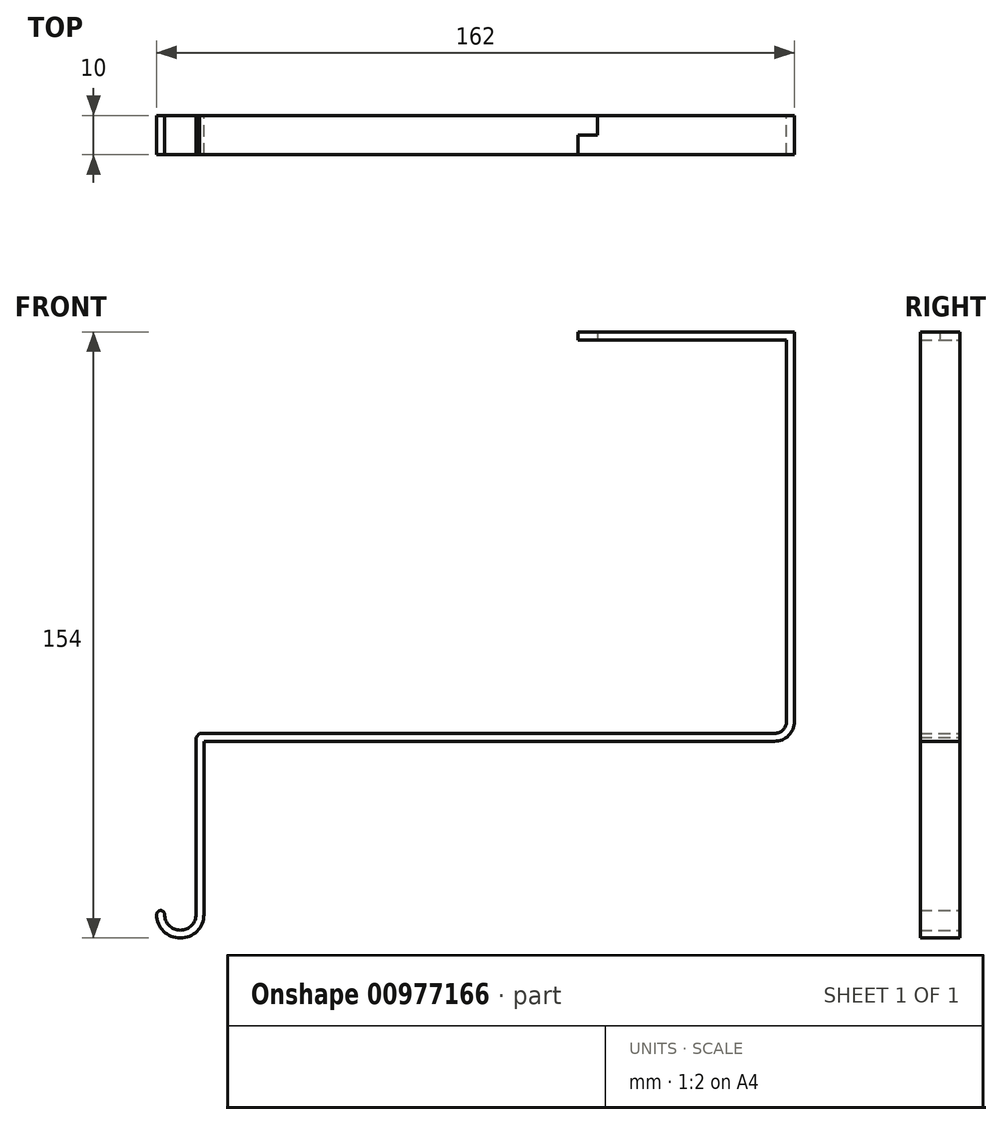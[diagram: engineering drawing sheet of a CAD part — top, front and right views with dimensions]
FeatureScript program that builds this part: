
annotation { "Feature Type Name" : "Feature", "Feature Type Description" : "" }
export const myFeature = defineFeature(function(context is Context, id is Id, definition is map)
    precondition{}
    {
        {
            var Q0;
            Q0=qCreatedBy(makeId("Front.planeOp"),FACE);
            var sketch = newSketch(context, id + "F0", { "sketchPlane" : qUnion([Q0])});
            skLineSegment(sketch, "E0", {"start": v(53.77, 110.57) * mm, "end": v(103.77, 110.57) * mm});
            skLineSegment(sketch, "E1", {"start": v(103.77, 110.57) * mm, "end": v(103.77, 11.57) * mm});
            skLineSegment(sketch, "E2", {"start": v(98.77, 6.57) * mm, "end": v(-46.23, 6.57) * mm});
            skLineSegment(sketch, "E3", {"start": v(-46.23, 6.57) * mm, "end": v(-46.23, -37.43) * mm});
            skArc(sketch, "E4", {"start": v(-46.23, -37.43) * mm, "mid": v(-52.23, -43.43) * mm, "end": v(-58.23, -37.43) * mm});
            skPoint(sketch, "E5.visualSharp", {"position": v(103.77, 6.57) * mm});
            skArc(sketch, "E5.filletArc", {"start": v(98.77, 6.57) * mm, "mid": v(102.3, 8.03) * mm, "end": v(103.77, 11.57) * mm});
            skLineSegment(sketch, "E6", {"start": v(53.77, 110.57) * mm, "end": v(48.77, 110.57) * mm});
            skLineSegment(sketch, "E7.0", {"start": v(-48.23, 7.5) * mm, "end": v(-48.23, -37.43) * mm});
            skLineSegment(sketch, "E7.1", {"start": v(53.77, 108.57) * mm, "end": v(48.77, 108.57) * mm});
            skLineSegment(sketch, "E7.2", {"start": v(53.77, 108.57) * mm, "end": v(101.77, 108.57) * mm});
            skLineSegment(sketch, "E7.3", {"start": v(101.77, 108.57) * mm, "end": v(101.77, 11.57) * mm});
            skLineSegment(sketch, "E7.4", {"start": v(98.77, 8.57) * mm, "end": v(-47.32, 8.57) * mm});
            skLineSegment(sketch, "E8", {"start": v(48.77, 110.57) * mm, "end": v(48.77, 108.57) * mm});
            skLineSegment(sketch, "E9", {"start": v(53.77, 110.57) * mm, "end": v(53.77, 108.57) * mm});
            skArc(sketch, "E10.0", {"start": v(-48.23, -37.43) * mm, "mid": v(-52.23, -41.43) * mm, "end": v(-56.23, -37.43) * mm});
            skArc(sketch, "E11", {"start": v(-58.23, -37.43) * mm, "mid": v(-57.23, -36.43) * mm, "end": v(-56.23, -37.43) * mm});
            skLineSegment(sketch, "E12", {"start": v(-47.32, 8.57) * mm, "end": v(-48.23, 7.5) * mm});
            skPoint(sketch, "E13.visualSharp", {"position": v(101.77, 8.57) * mm});
            skArc(sketch, "E13.filletArc", {"start": v(98.77, 8.57) * mm, "mid": v(100.9, 9.45) * mm, "end": v(101.77, 11.57) * mm});
            skSolve(sketch);
        }
        {
            var Q0;
            Q0=makeQuery(id+"F0.imprint","IMPRINT",FACE,{"disambiguationData":[TD([[makeQuery(id+"F0.imprint","IMPRINT",EDGE,{"derivedFrom":sQuery(id+"F0.wireOp",EDGE,"E0")}),-1.0]])]});
            extrude(context, id + "F1", {"entities" : qUnion([Q0]), "depth" : 10 * mm, "offsetDistance" : 25 * mm, "symmetric" : true});
        }
        {
            var Q0;
            Q0=makeQuery(id+"F0.imprint","IMPRINT",FACE,{"disambiguationData":[TD([[makeQuery(id+"F0.imprint","IMPRINT",EDGE,{"derivedFrom":sQuery(id+"F0.wireOp",EDGE,"E6")}),1.0]])]});
            extrude(context, id + "F2", {"entities" : qUnion([Q0]), "operationType" : NewBodyOperationType.ADD, "depth" : 5 * mm, "offsetDistance" : 25 * mm});
        }
    });
